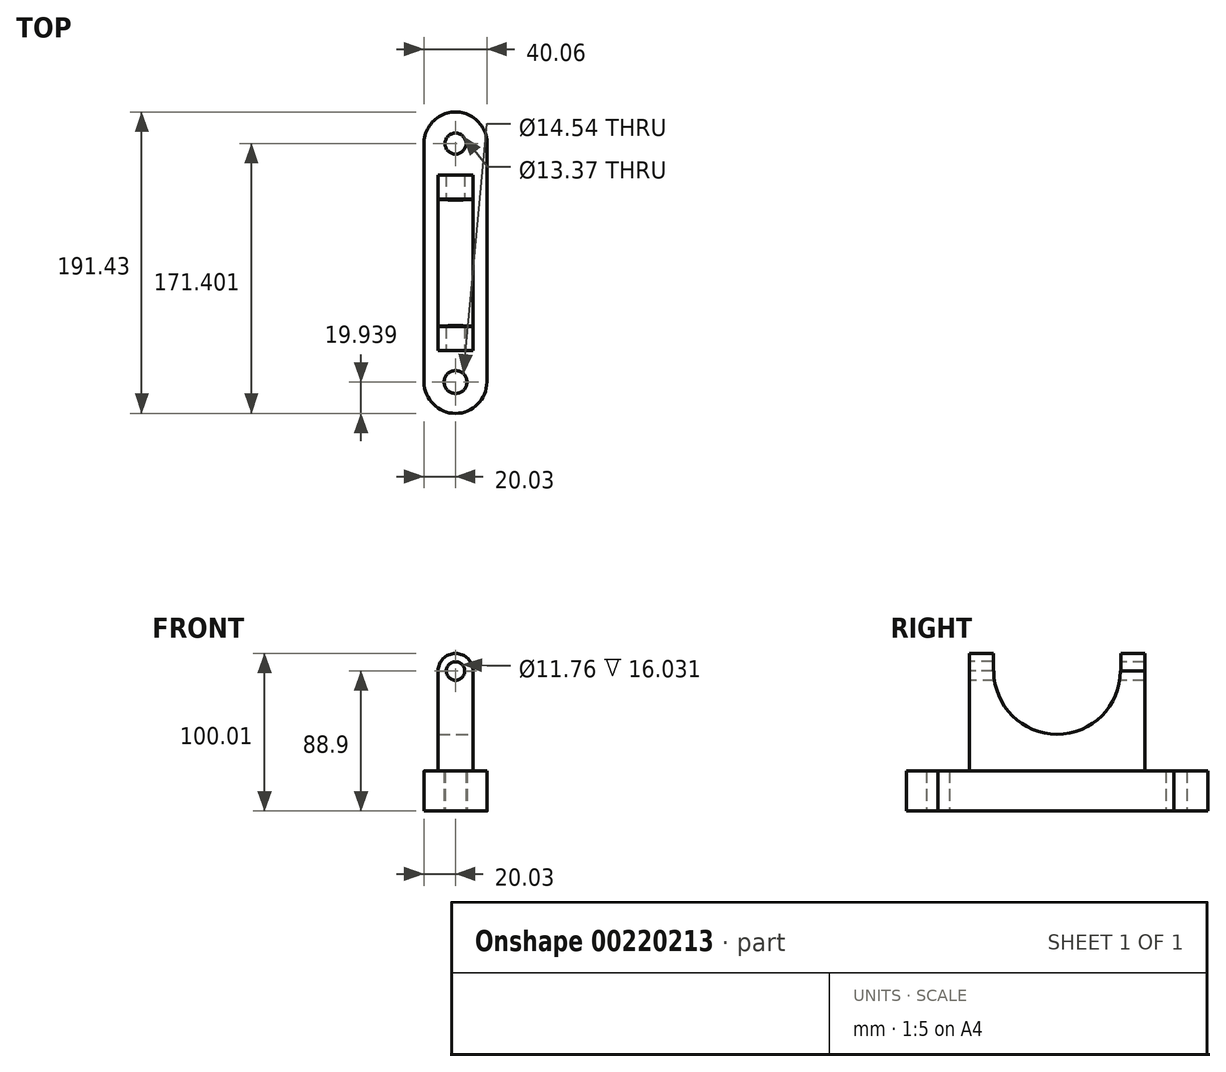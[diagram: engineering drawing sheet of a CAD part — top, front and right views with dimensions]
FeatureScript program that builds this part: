
annotation { "Feature Type Name" : "Feature", "Feature Type Description" : "" }
export const myFeature = defineFeature(function(context is Context, id is Id, definition is map)
    precondition{}
    {
        {
            var Q0;
            Q0=qCreatedBy(makeId("Top.planeOp"),FACE);
            var sketch = newSketch(context, id + "F0", { "sketchPlane" : qUnion([Q0])});
            skLineSegment(sketch, "E0.top", {"start": v(-19.97, -75.73) * mm, "end": v(-19.94, -75.73) * mm});
            skLineSegment(sketch, "E0.left", {"start": v(-19.97, 75.73) * mm, "end": v(-19.97, -75.73) * mm});
            skLineSegment(sketch, "E0.right", {"start": v(19.97, 75.73) * mm, "end": v(19.97, -75.73) * mm});
            skPoint(sketch, "E0.middle", {"position": v(0, 0) * mm});
            skArc(sketch, "E1", {"start": v(-19.94, -75.73) * mm, "mid": v(0, -95.67) * mm, "end": v(19.94, -75.73) * mm});
            skArc(sketch, "E2", {"start": v(19.97, 74.12) * mm, "mid": v(0, 95.76) * mm, "end": v(-19.97, 74.12) * mm});
            skLineSegment(sketch, "E3.trimOffspring", {"start": v(19.94, -75.73) * mm, "end": v(19.97, -75.73) * mm});
            skCircle(sketch, "E4", {"center": v(0, 75.73) * mm, "radius": 6.68 * mm});
            skCircle(sketch, "E5", {"center": v(0, -75.73) * mm, "radius": 7.27 * mm});
            skSolve(sketch);
        }
        {
            var Q0;
            Q0 = qSketchRegion(id + "F0", true);
            extrude(context, id + "F1", {"entities" : qUnion([Q0]), "depth" : 25.4 * mm});
        }
        {
            var Q0;
            Q0=makeQuery(id+"F1.opExtrude","CAP_FACE",FACE,{"disambiguationData":[OSD([sQuery(id+"F0.wireOp",EDGE,"E0.top"),sQuery(id+"F0.wireOp",EDGE,"E0.left"),sQuery(id+"F0.wireOp",EDGE,"E0.right"),sQuery(id+"F0.wireOp",EDGE,"E1"),sQuery(id+"F0.wireOp",EDGE,"E2"),sQuery(id+"F0.wireOp",EDGE,"E3.trimOffspring"),sQuery(id+"F0.wireOp",EDGE,"E4"),sQuery(id+"F0.wireOp",EDGE,"E5")])],"isStart":false});
            var sketch = newSketch(context, id + "F2", { "sketchPlane" : qUnion([Q0])});
            skLineSegment(sketch, "E6.bottom", {"start": v(-11.1, 55.76) * mm, "end": v(11.1, 55.76) * mm});
            skLineSegment(sketch, "E6.top", {"start": v(-11.1, -55.76) * mm, "end": v(11.1, -55.76) * mm});
            skLineSegment(sketch, "E6.left", {"start": v(-11.1, 55.76) * mm, "end": v(-11.1, -55.76) * mm});
            skLineSegment(sketch, "E6.right", {"start": v(11.1, 55.76) * mm, "end": v(11.1, -55.76) * mm});
            skPoint(sketch, "E6.middle", {"position": v(0, 0) * mm});
            skSolve(sketch);
        }
        {
            var Q0;
            Q0=makeQuery(id+"F2.imprint","IMPRINT",FACE,{"disambiguationData":[TD([[makeQuery(id+"F2.imprint","IMPRINT",EDGE,{"derivedFrom":sQuery(id+"F2.wireOp",EDGE,"E6.bottom")}),-1.0]])]});
            extrude(context, id + "F3", {"entities" : qUnion([Q0]), "operationType" : NewBodyOperationType.ADD, "depth" : 63.5 * mm});
        }
        {
            var Q0;
            Q0=makeQuery(id+"F3.opExtrude","SWEPT_FACE",FACE,{"disambiguationData":[OSD([sQuery(id+"F2.wireOp",EDGE,"E6.right")])]});
            var sketch = newSketch(context, id + "F4", { "sketchPlane" : qUnion([Q0])});
            skArc(sketch, "E7", {"start": v(-40.17, 88.9) * mm, "mid": v(0, 48.73) * mm, "end": v(40.17, 88.9) * mm});
            skLineSegment(sketch, "E8", {"start": v(-40.17, 88.9) * mm, "end": v(40.17, 88.9) * mm});
            skSolve(sketch);
        }
        {
            var Q0;
            Q0 = qSketchRegion(id + "F4", true);
            extrude(context, id + "F5", {"entities" : qUnion([Q0]), "operationType" : NewBodyOperationType.REMOVE, "endBound" : BoundingType.THROUGH_ALL, "oppositeDirection" : true, "depth" : 25.4 * mm});
        }
        {
            var Q0;
            Q0=makeQuery(id+"F3.opExtrude","SWEPT_FACE",FACE,{"disambiguationData":[OSD([sQuery(id+"F2.wireOp",EDGE,"E6.top")])]});
            var sketch = newSketch(context, id + "F6", { "sketchPlane" : qUnion([Q0])});
            skArc(sketch, "E9", {"start": v(11.1, 88.9) * mm, "mid": v(0, 100) * mm, "end": v(-11.1, 88.9) * mm});
            skCircle(sketch, "E10", {"center": v(0, 88.9) * mm, "radius": 5.92 * mm});
            skSolve(sketch);
        }
        {
            var Q0;
            {var subQ0=sQuery(id+"F6.wireOp",EDGE,"E9");Q0=makeQuery(id+"F6.imprint","IMPRINT",FACE,{"disambiguationData":[TD([[makeQuery(id+"F6.imprint","IMPRINT",EDGE,{"derivedFrom":subQ0}),1.0]])]});}
            extrude(context, id + "F7", {"entities" : qUnion([Q0]), "operationType" : NewBodyOperationType.ADD, "oppositeDirection" : true, "depth" : 15.24 * mm});
        }
        {
            var Q0;
            Q0=makeQuery(id+"F3.opExtrude","SWEPT_FACE",FACE,{"disambiguationData":[OSD([sQuery(id+"F2.wireOp",EDGE,"E6.bottom")])]});
            var sketch = newSketch(context, id + "F8", { "sketchPlane" : qUnion([Q0])});
            skArc(sketch, "E11", {"start": v(11.07, 88.9) * mm, "mid": v(0, 99.97) * mm, "end": v(-11.07, 88.9) * mm});
            skLineSegment(sketch, "E12", {"start": v(-11.1, 88.9) * mm, "end": v(11.1, 88.9) * mm});
            skSolve(sketch);
        }
        {
            var Q0;
            Q0 = qSketchRegion(id + "F8", true);
            extrude(context, id + "F9", {"entities" : qUnion([Q0]), "operationType" : NewBodyOperationType.ADD, "oppositeDirection" : true, "depth" : 15.24 * mm});
        }
        {
            var Q0;
            {var subQ0=sQuery(id+"F2.wireOp",EDGE,"E6.top");Q0=makeQuery(id+"F7.boolean.opBoolean","MERGE",FACE,{"derivedFrom":[makeQuery(id+"F3.opExtrude","SWEPT_FACE",FACE,{"disambiguationData":[OSD([subQ0])]}),makeQuery(id+"F7.opExtrude","CAP_FACE",FACE,{"disambiguationData":[OSD([subQ0,sQuery(id+"F6.wireOp",EDGE,"E9"),sQuery(id+"F6.wireOp",EDGE,"E10")])],"isStart":true})]});}
            var sketch = newSketch(context, id + "F10", { "sketchPlane" : qUnion([Q0])});
            skCircle(sketch, "E13", {"center": v(0, 88.9) * mm, "radius": 5.88 * mm});
            skSolve(sketch);
        }
        {
            var Q0;
            Q0 = qSketchRegion(id + "F10", true);
            extrude(context, id + "F11", {"entities" : qUnion([Q0]), "operationType" : NewBodyOperationType.REMOVE, "endBound" : BoundingType.THROUGH_ALL, "oppositeDirection" : true, "depth" : 25.4 * mm});
        }
    });
